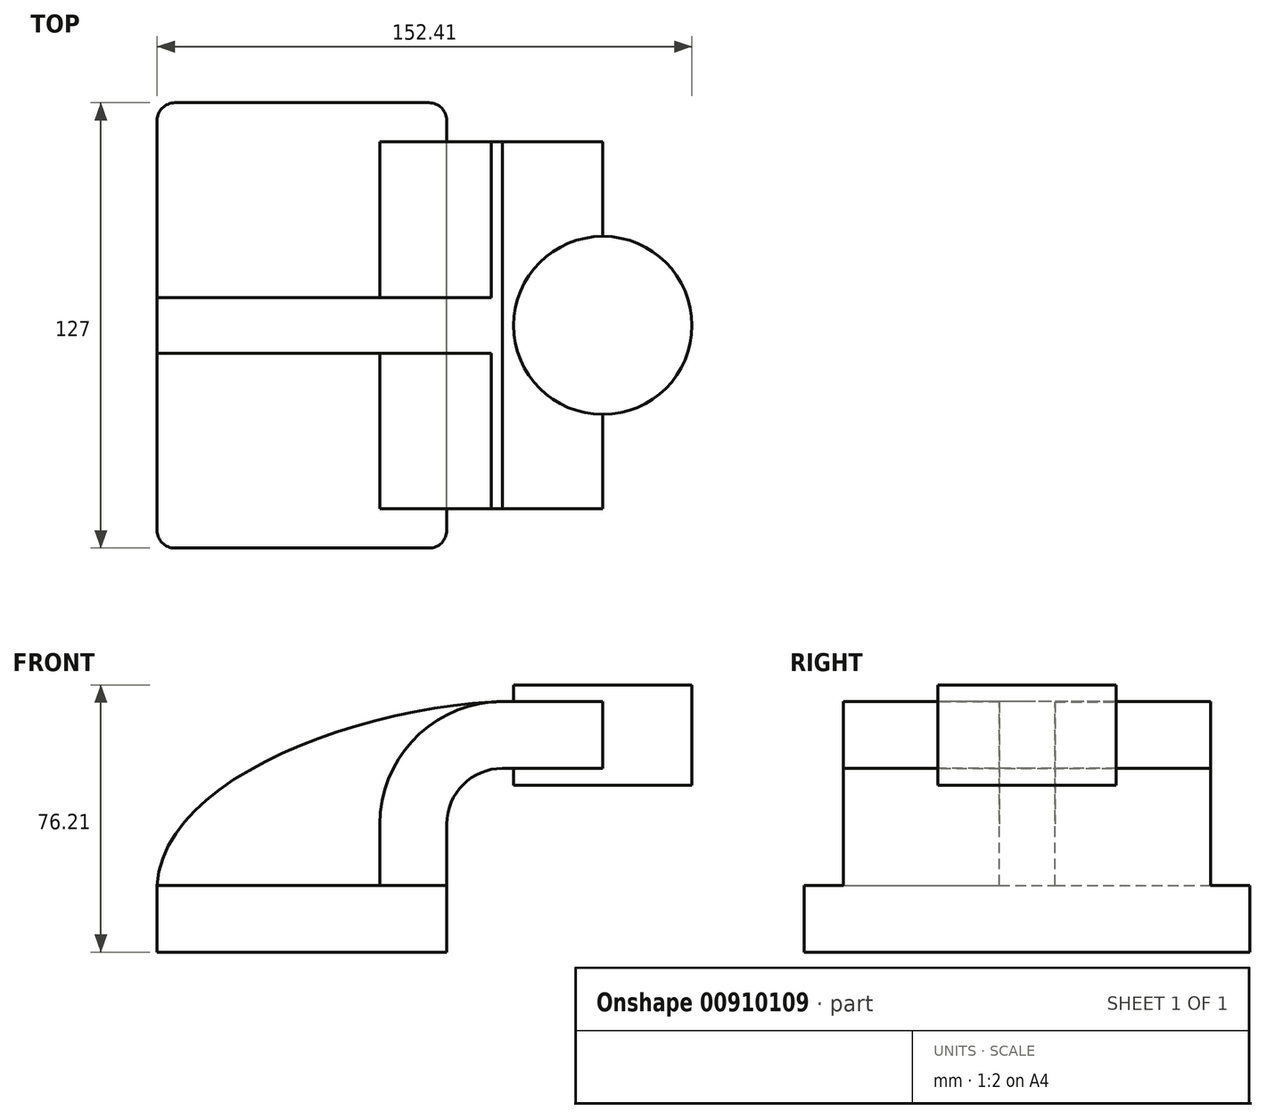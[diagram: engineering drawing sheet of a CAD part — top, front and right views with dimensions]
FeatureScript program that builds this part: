
annotation { "Feature Type Name" : "Feature", "Feature Type Description" : "" }
export const myFeature = defineFeature(function(context is Context, id is Id, definition is map)
    precondition{}
    {
        {
            var Q0;
            Q0=qCreatedBy(makeId("Front.planeOp"),FACE);
            var sketch = newSketch(context, id + "F0", { "sketchPlane" : qUnion([Q0])});
            skLineSegment(sketch, "E0.rect.bottom", {"start": v(-41.28, 9.52) * mm, "end": v(41.28, 9.52) * mm});
            skLineSegment(sketch, "E0.rect.top", {"start": v(-41.28, -9.52) * mm, "end": v(41.28, -9.52) * mm});
            skLineSegment(sketch, "E0.rect.left", {"start": v(-41.28, 9.52) * mm, "end": v(-41.28, -9.52) * mm});
            skLineSegment(sketch, "E0.rect.right", {"start": v(41.28, 9.52) * mm, "end": v(41.28, -9.52) * mm});
            skPoint(sketch, "E0.rect.middle", {"position": v(0, 0) * mm});
            skLineSegment(sketch, "E1", {"start": v(41.28, 9.52) * mm, "end": v(41.28, 27) * mm});
            skArc(sketch, "E2", {"start": v(41.28, 27) * mm, "mid": v(45.92, 38.23) * mm, "end": v(57.15, 42.88) * mm});
            skLineSegment(sketch, "E3", {"start": v(57.15, 42.88) * mm, "end": v(85.72, 42.88) * mm});
            skLineSegment(sketch, "E4.rect.bottom", {"start": v(60.32, 38.1) * mm, "end": v(111.12, 38.1) * mm});
            skLineSegment(sketch, "E4.rect.top", {"start": v(60.32, 66.68) * mm, "end": v(111.12, 66.68) * mm});
            skLineSegment(sketch, "E4.rect.left", {"start": v(60.32, 38.1) * mm, "end": v(60.32, 66.68) * mm});
            skLineSegment(sketch, "E4.rect.right", {"start": v(111.13, 38.1) * mm, "end": v(111.12, 66.68) * mm});
            skPoint(sketch, "E4.rect.middle", {"position": v(85.72, 52.39) * mm});
            skLineSegment(sketch, "E5.0", {"start": v(57.15, 61.93) * mm, "end": v(85.72, 61.93) * mm});
            skArc(sketch, "E5.1", {"start": v(22.23, 27) * mm, "mid": v(32.45, 51.7) * mm, "end": v(57.15, 61.93) * mm});
            skLineSegment(sketch, "E5.2", {"start": v(22.23, 9.52) * mm, "end": v(22.23, 27) * mm});
            skLineSegment(sketch, "E6", {"start": v(85.72, 38.1) * mm, "end": v(85.72, 66.68) * mm});
            skFitSpline(sketch, "E7", {"points": [v(-41.28, 9.53) * mm, v(57.15, 61.93) * mm], "startDerivative": vector(5.2, 92.34) * mm, "endDerivative": vector(120.92, 4.22) * mm});
            skSolve(sketch);
        }
        {
            var Q0;
            Q0=makeQuery(id+"F0.imprint","IMPRINT",FACE,{"disambiguationData":[TD([[makeQuery(id+"F0.imprint","IMPRINT",EDGE,{"derivedFrom":sQuery(id+"F0.wireOp",EDGE,"E0.rect.top")}),1.0]])]});
            extrude(context, id + "F1", {"entities" : qUnion([Q0]), "endBound" : BoundingType.SYMMETRIC, "offsetDistance" : 25.4 * mm, "depth" : 127 * mm});
        }
        {
            var Q0;
            {var subQ9=sQuery(id+"F0.wireOp",EDGE,"E1");Q0=makeQuery(id+"F0.imprint","IMPRINT",FACE,{"disambiguationData":[TD([[makeQuery(id+"F0.imprint","IMPRINT",EDGE,{"derivedFrom":subQ9}),1.0]])]});}
            var Q1;
            {var subQ0=sQuery(id+"F0.wireOp",EDGE,"E6");var subQ1=sQuery(id+"F0.wireOp",EDGE,"E3");var subQ2=makeQuery(id+"F0.imprint","INTERSECT",VERTEX,{"derivedFrom":[subQ1,subQ0]});Q1=makeQuery(id+"F0.imprint","IMPRINT",FACE,{"disambiguationData":[TD([[makeQuery(id+"F0.imprint","IMPRINT",EDGE,{"disambiguationData":[TD([[subQ2,1.0]])],"derivedFrom":subQ1}),1.0]])]});}
            extrude(context, id + "F2", {"entities" : qUnion([Q0, Q1]), "operationType" : NewBodyOperationType.ADD, "endBound" : BoundingType.SYMMETRIC, "offsetDistance" : 25.4 * mm, "depth" : 104.65 * mm});
        }
        {
            var Q0;
            {var subQ3=sQuery(id+"F0.wireOp",EDGE,"E5.2");Q0=makeQuery(id+"F0.imprint","IMPRINT",FACE,{"disambiguationData":[TD([[makeQuery(id+"F0.imprint","IMPRINT",EDGE,{"derivedFrom":subQ3}),1.0]])]});}
            extrude(context, id + "F3", {"entities" : qUnion([Q0]), "operationType" : NewBodyOperationType.ADD, "endBound" : BoundingType.SYMMETRIC, "depth" : 15.88 * mm});
        }
        {
            var Q0;
            {var subQ5=sQuery(id+"F0.wireOp",EDGE,"E4.rect.right");Q0=makeQuery(id+"F0.imprint","IMPRINT",FACE,{"disambiguationData":[TD([[makeQuery(id+"F0.imprint","IMPRINT",EDGE,{"derivedFrom":subQ5}),1.0]])]});}
            var Q1;
            Q1=sQuery(id+"F0.wireOp",EDGE,"E6");
            revolve(context, id + "F4", {"operationType" : NewBodyOperationType.ADD, "entities" : qUnion([Q0]), "axis" : qUnion([Q1]), "revolveType" : RevolveType.FULL});
        }
        {
            var Q0;
            Q0=makeQuery(id+"F1.opExtrude","CAP_EDGE",EDGE,{"disambiguationData":[OSD([sQuery(id+"F0.wireOp",EDGE,"E0.rect.right")])],"isStart":false});
            var Q1;
            Q1=makeQuery(id+"F1.opExtrude","CAP_EDGE",EDGE,{"disambiguationData":[OSD([sQuery(id+"F0.wireOp",EDGE,"E0.rect.left")])],"isStart":false});
            var Q2;
            Q2=makeQuery(id+"F1.opExtrude","CAP_EDGE",EDGE,{"disambiguationData":[OSD([sQuery(id+"F0.wireOp",EDGE,"E0.rect.right")])],"isStart":true});
            var Q3;
            Q3=makeQuery(id+"F1.opExtrude","CAP_EDGE",EDGE,{"disambiguationData":[OSD([sQuery(id+"F0.wireOp",EDGE,"E0.rect.left")])],"isStart":true});
            fillet(context, id + "F5", {"entities" : qUnion([Q0, Q1, Q2, Q3]), "radius" : 5.08 * mm, "tangentPropagation" : true, "allowEdgeOverflow" : false});
        }
    });
